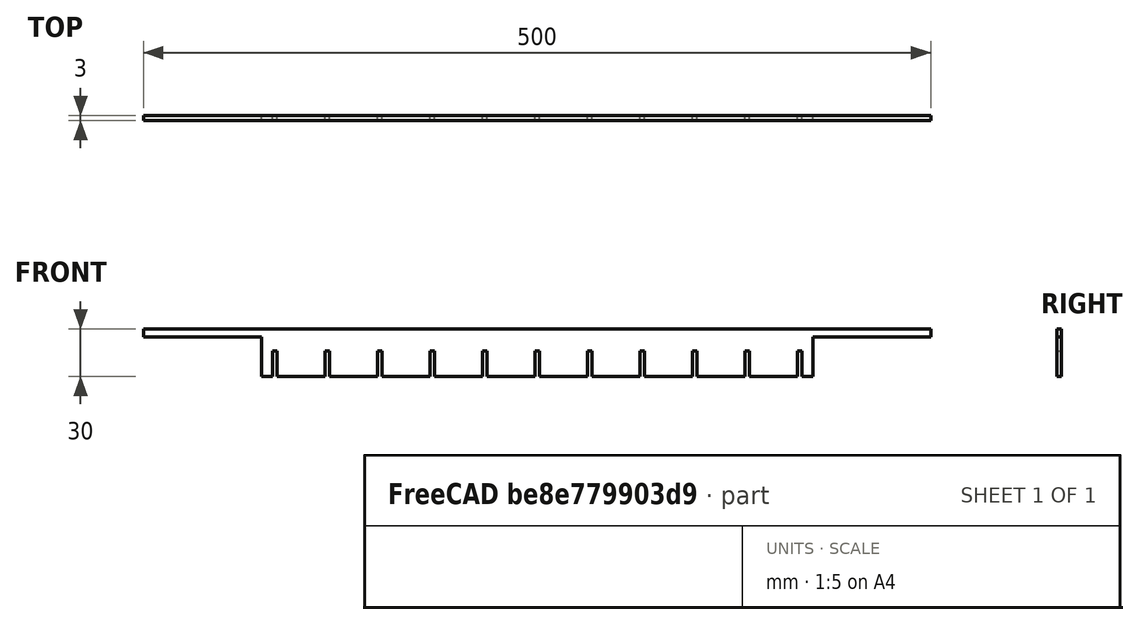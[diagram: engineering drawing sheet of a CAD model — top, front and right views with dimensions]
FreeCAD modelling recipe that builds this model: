
FCSTD DOCUMENT  (FreeCAD 0.16R6527 (Git))
Label: strip_333
License: CC-BY 3.0
LicenseURL: http://creativecommons.org/licenses/by/3.0/
objects: Part::Box×3, Part::FeaturePython×2, Part::Cut×2
note: 7 computed .brp shape members not serialized (recipe doc carries the construction recipe); baked Part::Feature solids carry a one-line shape summary decoded from their .brp

FEATURE [Part::Box] Box  label="Strip"
  Height = 30
  Length = 500
  Width = 3
  expr: Height = strip_500#Strip.Height
  expr: Width = strip_500#Strip.Width
  expr: Length = bottom#Slab.Width - 2 * bottom#Slab.Height
FEATURE [Part::Box] Box001  label="Hole"
  Height = 16
  Length = 3
  Width = 3
  expr: Placement.Base.x = 0
  expr: Height = Strip.Height / 2 + 1mm
  expr: Length = Strip.Width
  expr: Width = Strip.Width
FEATURE [Part::FeaturePython] Array  # Draft array (typed FeaturePython)
  Angle = 360
  ArrayType = 0
  Axis = (1,0,0)
  Base = -> Box001
  Center = (0,0,0)
  IntervalX = (33.3333,0,0)
  IntervalY = (0,1,0)
  IntervalZ = (0,0,1)
  NumberPolar = 1
  NumberX = 11
  NumberY = 0
  NumberZ = 0
  Placement = pos=(81.8333,0,0) rot=(0,0,1;0rad)
  expr: Placement.Base.x = (Strip.Length - 1000mm / 3) / 2 - Strip.Width / 2
  expr: IntervalX.x = 100 / 3
FEATURE [Part::Cut] Cut  label="Horizontal_Cut"
  Base = -> Box
  Tool = -> Array
FEATURE [Part::Box] Box002  label="Hollow"
  Height = 25
  Length = 75
  Width = 10
  expr: Length = 75
  expr: Height = Strip.Height - 5mm
FEATURE [Part::FeaturePython] Array002  label="Hollow_Array"  # Draft array (typed FeaturePython)
  Angle = 360
  ArrayType = 0
  Axis = (0,0,1)
  Base = -> Box002
  Center = (0,0,0)
  Fuse = false
  IntervalAxis = (0,0,0)
  IntervalX = (425,0,0)
  IntervalY = (0,1,0)
  IntervalZ = (0,0,0)
  NumberPolar = 1
  NumberX = 2
  NumberY = 1
  NumberZ = 1
  expr: IntervalX.x = Strip.Length - Hollow.Length
FEATURE [Part::Cut] Cut001  label="Cut"
  Base = -> Cut
  Tool = -> Array002
